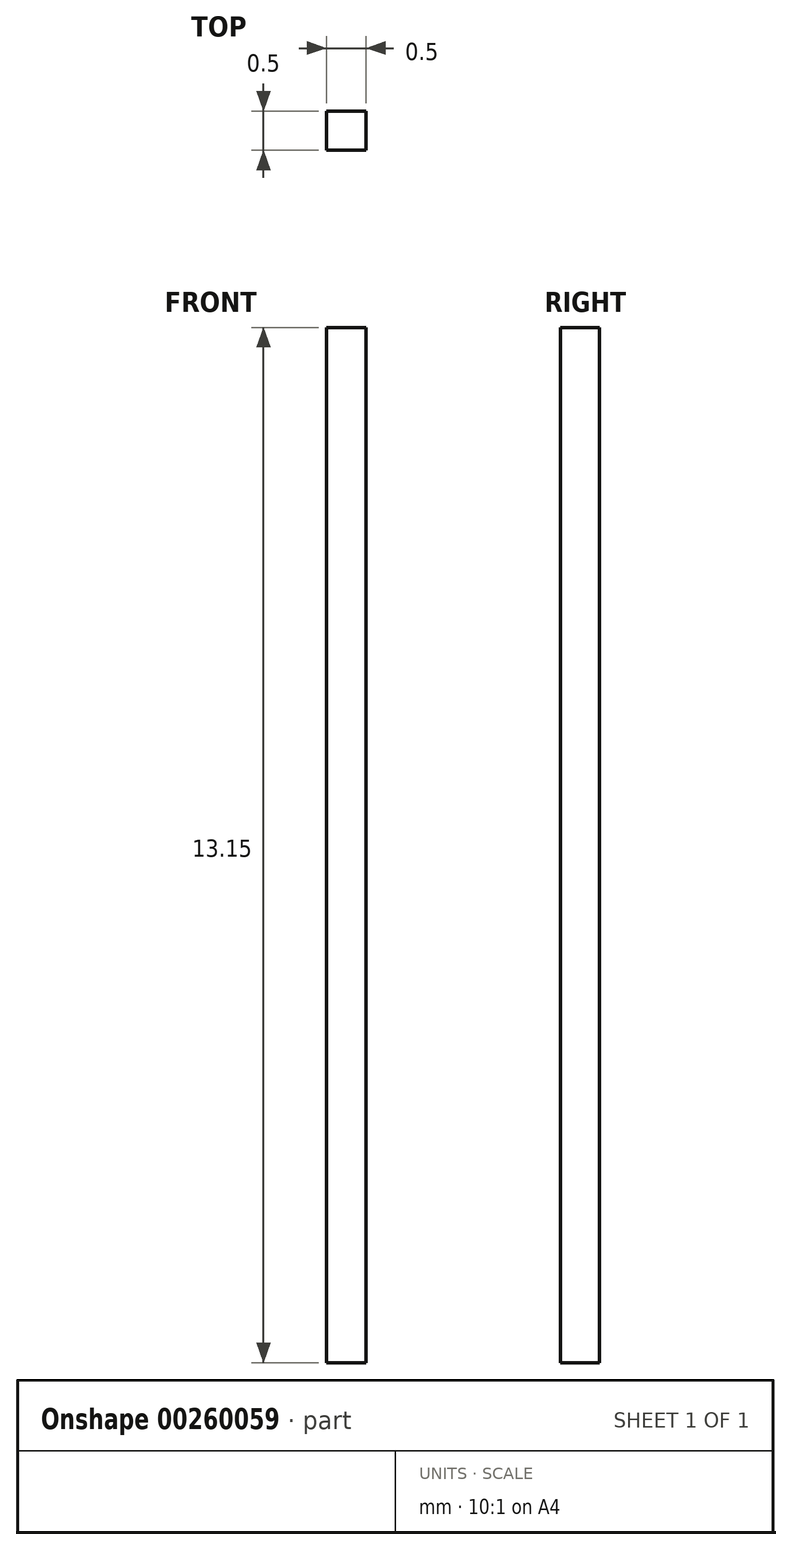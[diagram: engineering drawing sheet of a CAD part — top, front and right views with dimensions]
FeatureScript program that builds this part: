
annotation { "Feature Type Name" : "Feature", "Feature Type Description" : "" }
export const myFeature = defineFeature(function(context is Context, id is Id, definition is map)
    precondition{}
    {
        {
            var Q0;
            Q0=qCreatedBy(makeId("Top.planeOp"),FACE);
            var sketch = newSketch(context, id + "F0", { "sketchPlane" : qUnion([Q0])});
            skLineSegment(sketch, "E0.bottom", {"start": v(0, 0) * mm, "end": v(0.5, 0) * mm});
            skLineSegment(sketch, "E0.top", {"start": v(0, 0.5) * mm, "end": v(0.5, 0.5) * mm});
            skLineSegment(sketch, "E0.left", {"start": v(0, 0) * mm, "end": v(0, 0.5) * mm});
            skLineSegment(sketch, "E0.right", {"start": v(0.5, 0) * mm, "end": v(0.5, 0.5) * mm});
            skSolve(sketch);
        }
        {
            var Q0;
            Q0=qSketchRegion(id+"F0",true);
            extrude(context, id + "F1", {"entities" : qUnion([Q0]), "depth" : 13.15 * mm});
        }
    });
